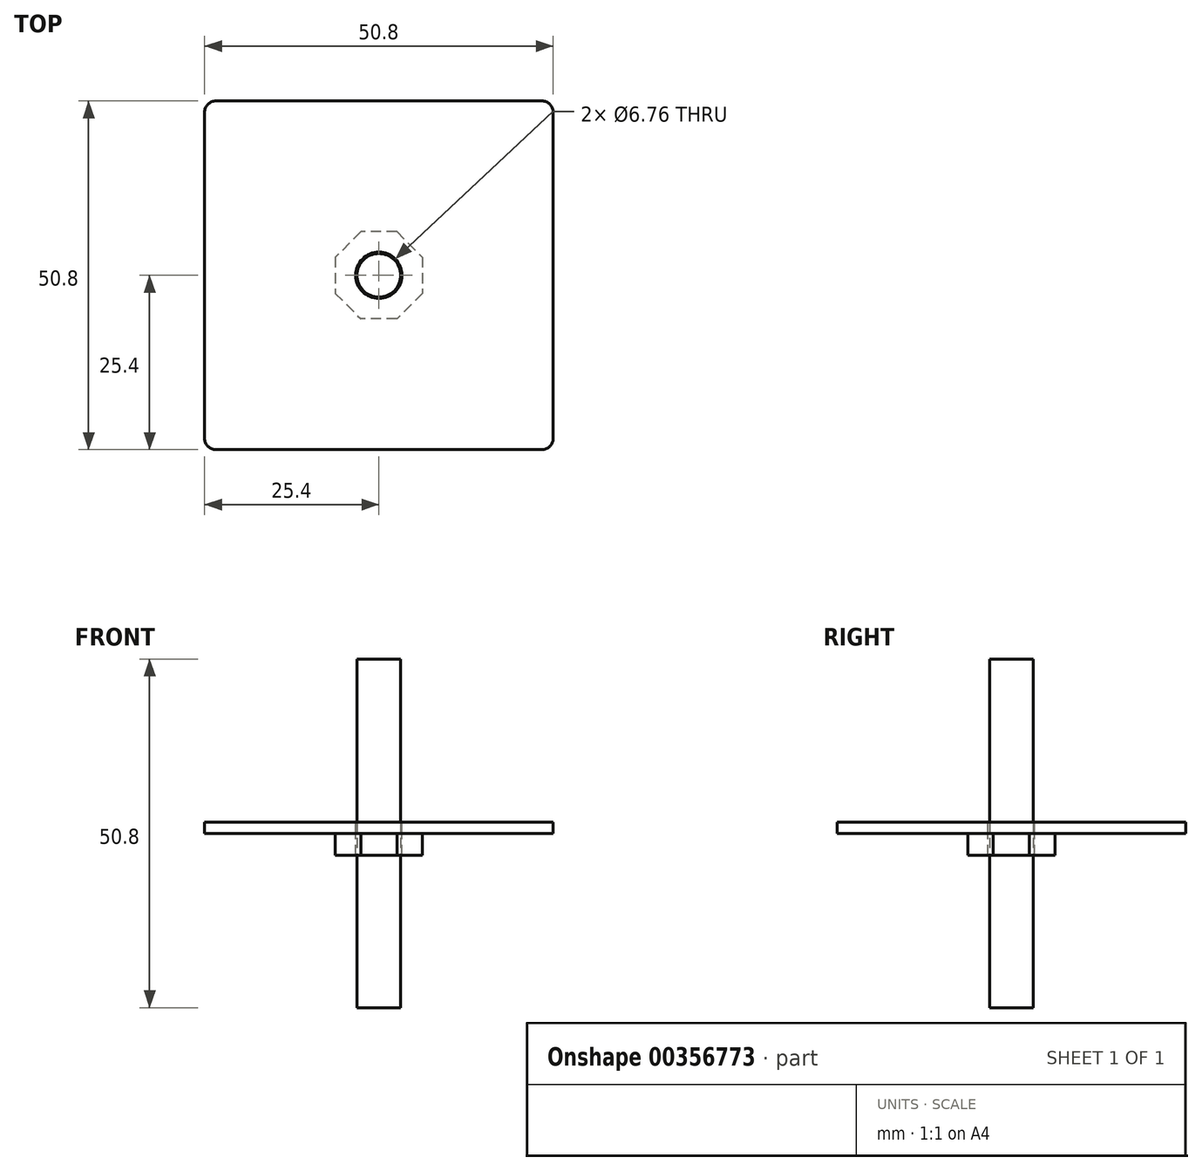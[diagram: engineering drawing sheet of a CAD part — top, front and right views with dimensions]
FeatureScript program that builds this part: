
annotation { "Feature Type Name" : "Feature", "Feature Type Description" : "" }
export const myFeature = defineFeature(function(context is Context, id is Id, definition is map)
    precondition{}
    {
        {
            var Q0;
            Q0=qCreatedBy(makeId("Top.planeOp"),FACE);
            var sketch = newSketch(context, id + "F0", { "sketchPlane" : qUnion([Q0])});
            skLineSegment(sketch, "E0.bottom", {"start": v(25.4, -25.4) * mm, "end": v(-25.4, -25.4) * mm});
            skLineSegment(sketch, "E0.top", {"start": v(25.4, 25.4) * mm, "end": v(-25.4, 25.4) * mm});
            skLineSegment(sketch, "E0.left", {"start": v(25.4, -25.4) * mm, "end": v(25.4, 25.4) * mm});
            skLineSegment(sketch, "E0.right", {"start": v(-25.4, -25.4) * mm, "end": v(-25.4, 25.4) * mm});
            skPoint(sketch, "E0.middle", {"position": v(0, 0) * mm});
            skSolve(sketch);
        }
        {
            var Q0;
            Q0=makeQuery(id+"F0.imprint","IMPRINT",FACE,{"disambiguationData":[TD([[makeQuery(id+"F0.imprint","IMPRINT",EDGE,{"derivedFrom":sQuery(id+"F0.wireOp",EDGE,"E0.bottom")}),-1.0]])]});
            extrude(context, id + "F1", {"entities" : qUnion([Q0]), "depth" : 1.65 * mm});
        }
        {
            var Q0;
            Q0=makeQuery(id+"F1.opExtrude","CAP_FACE",FACE,{"disambiguationData":[OSD([sQuery(id+"F0.wireOp",EDGE,"E0.bottom"),sQuery(id+"F0.wireOp",EDGE,"E0.top"),sQuery(id+"F0.wireOp",EDGE,"E0.left"),sQuery(id+"F0.wireOp",EDGE,"E0.right")])],"isStart":false});
            var sketch = newSketch(context, id + "F2", { "sketchPlane" : qUnion([Q0])});
            skPoint(sketch, "E1", {"position": v(0, 0) * mm});
            skSolve(sketch);
        }
        {
            var Q0;
            Q0=sQuery(id+"F2.wireOp",VERTEX,"E1");
            var Q1;
            Q1=makeQuery(id+"F1.opExtrude","SWEPT_BODY",BODY,{"disambiguationData":[OSD([sQuery(id+"F0.wireOp",EDGE,"E0.bottom"),sQuery(id+"F0.wireOp",EDGE,"E0.top"),sQuery(id+"F0.wireOp",EDGE,"E0.left"),sQuery(id+"F0.wireOp",EDGE,"E0.right")])]});
            hole(context, id + "F3", {"style" : HoleStyle.SIMPLE, "endStyle" : HoleEndStyle.BLIND, "standardTappedOrClearance" : lookupTablePath({ "standard" : "ANSI", "fit" : "Normal (ASME)", "size" : "1/4", "type" : "Clearance" }), "standardBlindInLast" : lookupTablePath({ "fit" : "Free", "standard" : "ANSI", "size" : "1/4", "type" : "Clearance" }), "holeDiameter" : 6.76 * mm, "holeDepth" : 25.4 * mm, "isTappedThrough" : true, "tappedDepth" : 12.7 * mm, "tapClearance" : 3, "locations" : qUnion([Q0]), "scope" : qUnion([Q1])});
        }
        {
            var Q0;
            Q0=makeQuery(id+"F1.opExtrude","CAP_FACE",FACE,{"disambiguationData":[OSD([sQuery(id+"F0.wireOp",EDGE,"E0.bottom"),sQuery(id+"F0.wireOp",EDGE,"E0.top"),sQuery(id+"F0.wireOp",EDGE,"E0.left"),sQuery(id+"F0.wireOp",EDGE,"E0.right")])],"isStart":true});
            var sketch = newSketch(context, id + "F4", { "sketchPlane" : qUnion([Q0])});
            skLineSegment(sketch, "E2.bottom", {"start": v(6.35, -6.35) * mm, "end": v(-6.35, -6.35) * mm});
            skLineSegment(sketch, "E2.top", {"start": v(6.35, 6.35) * mm, "end": v(-6.35, 6.35) * mm});
            skLineSegment(sketch, "E2.left", {"start": v(6.35, -6.35) * mm, "end": v(6.35, 6.35) * mm});
            skLineSegment(sketch, "E2.right", {"start": v(-6.35, -6.35) * mm, "end": v(-6.35, 6.35) * mm});
            skLineSegment(sketch, "E3.bottom", {"start": v(0, -8.98) * mm, "end": v(-8.98, 0) * mm});
            skLineSegment(sketch, "E3.top", {"start": v(8.98, 0) * mm, "end": v(0, 8.98) * mm});
            skLineSegment(sketch, "E3.left", {"start": v(0, -8.98) * mm, "end": v(8.98, 0) * mm});
            skLineSegment(sketch, "E3.right", {"start": v(-8.98, 0) * mm, "end": v(0, 8.98) * mm});
            skPoint(sketch, "E3.middle", {"position": v(0, 0) * mm});
            skLineSegment(sketch, "E4", {"start": v(-8.98, 0) * mm, "end": v(8.98, 0) * mm});
            skSolve(sketch);
        }
        {
            var Q0;
            {var subQ5=sQuery(id+"F4.wireOp",EDGE,"E3.top");var subQ6=sQuery(id+"F4.wireOp",EDGE,"E2.top");var subQ7=makeQuery(id+"F4.imprint","INTERSECT",VERTEX,{"derivedFrom":[subQ6,subQ5]});Q0=makeQuery(id+"F4.imprint","IMPRINT",FACE,{"disambiguationData":[TD([[makeQuery(id+"F4.imprint","IMPRINT",EDGE,{"disambiguationData":[TD([[subQ7,-1.0]])],"derivedFrom":subQ6}),1.0]])]});}
            var Q1;
            {var subQ1=sQuery(id+"F4.wireOp",EDGE,"E2.bottom");var subQ5=sQuery(id+"F4.wireOp",EDGE,"E3.left");var subQ13=makeQuery(id+"F4.imprint","INTERSECT",VERTEX,{"derivedFrom":[subQ1,subQ5]});Q1=makeQuery(id+"F4.imprint","IMPRINT",FACE,{"disambiguationData":[TD([[makeQuery(id+"F4.imprint","IMPRINT",EDGE,{"disambiguationData":[TD([[subQ13,-1.0]])],"derivedFrom":subQ1}),-1.0]])]});}
            extrude(context, id + "F5", {"entities" : qUnion([Q0, Q1]), "depth" : 3.17 * mm});
        }
        {
            var Q0;
            Q0=qCreatedBy(makeId("Right.planeOp"),FACE);
            var sketch = newSketch(context, id + "F6", { "sketchPlane" : qUnion([Q0])});
            skLineSegment(sketch, "E5.bottom", {"start": v(-3.17, 25.4) * mm, "end": v(3.18, 25.4) * mm});
            skLineSegment(sketch, "E5.top", {"start": v(-3.18, -25.4) * mm, "end": v(3.17, -25.4) * mm});
            skLineSegment(sketch, "E5.left", {"start": v(-3.18, 25.4) * mm, "end": v(-3.18, -25.4) * mm});
            skLineSegment(sketch, "E5.right", {"start": v(3.18, 25.4) * mm, "end": v(3.17, -25.4) * mm});
            skPoint(sketch, "E5.middle", {"position": v(0, 0) * mm});
            skLineSegment(sketch, "E6", {"start": v(0, -25.4) * mm, "end": v(0, 25.4) * mm});
            skSolve(sketch);
        }
        {
            var Q0;
            {var subQ0=sQuery(id+"F6.wireOp",EDGE,"E5.left");Q0=makeQuery(id+"F6.imprint","IMPRINT",FACE,{"disambiguationData":[TD([[makeQuery(id+"F6.imprint","IMPRINT",EDGE,{"derivedFrom":subQ0}),1.0]])]});}
            var Q1;
            Q1=sQuery(id+"F6.wireOp",EDGE,"E6");
            revolve(context, id + "F7", {"entities" : qUnion([Q0]), "axis" : qUnion([Q1]), "revolveType" : RevolveType.FULL});
        }
        {
            var Q0;
            Q0=makeQuery(id+"F1.opExtrude","SWEPT_EDGE",EDGE,{"disambiguationData":[OSD([sQuery(id+"F0.wireOp",EDGE,"E0.bottom"),sQuery(id+"F0.wireOp",EDGE,"E0.right")])]});
            var Q1;
            Q1=makeQuery(id+"F1.opExtrude","SWEPT_EDGE",EDGE,{"disambiguationData":[OSD([sQuery(id+"F0.wireOp",EDGE,"E0.top"),sQuery(id+"F0.wireOp",EDGE,"E0.left")])]});
            var Q2;
            Q2=makeQuery(id+"F1.opExtrude","SWEPT_EDGE",EDGE,{"disambiguationData":[OSD([sQuery(id+"F0.wireOp",EDGE,"E0.top"),sQuery(id+"F0.wireOp",EDGE,"E0.right")])]});
            var Q3;
            Q3=makeQuery(id+"F1.opExtrude","SWEPT_EDGE",EDGE,{"disambiguationData":[OSD([sQuery(id+"F0.wireOp",EDGE,"E0.bottom"),sQuery(id+"F0.wireOp",EDGE,"E0.left")])]});
            fillet(context, id + "F8", {"entities" : qUnion([Q0, Q1, Q2, Q3]), "radius" : 1.65 * mm, "tangentPropagation" : true, "allowEdgeOverflow" : false});
        }
    });
